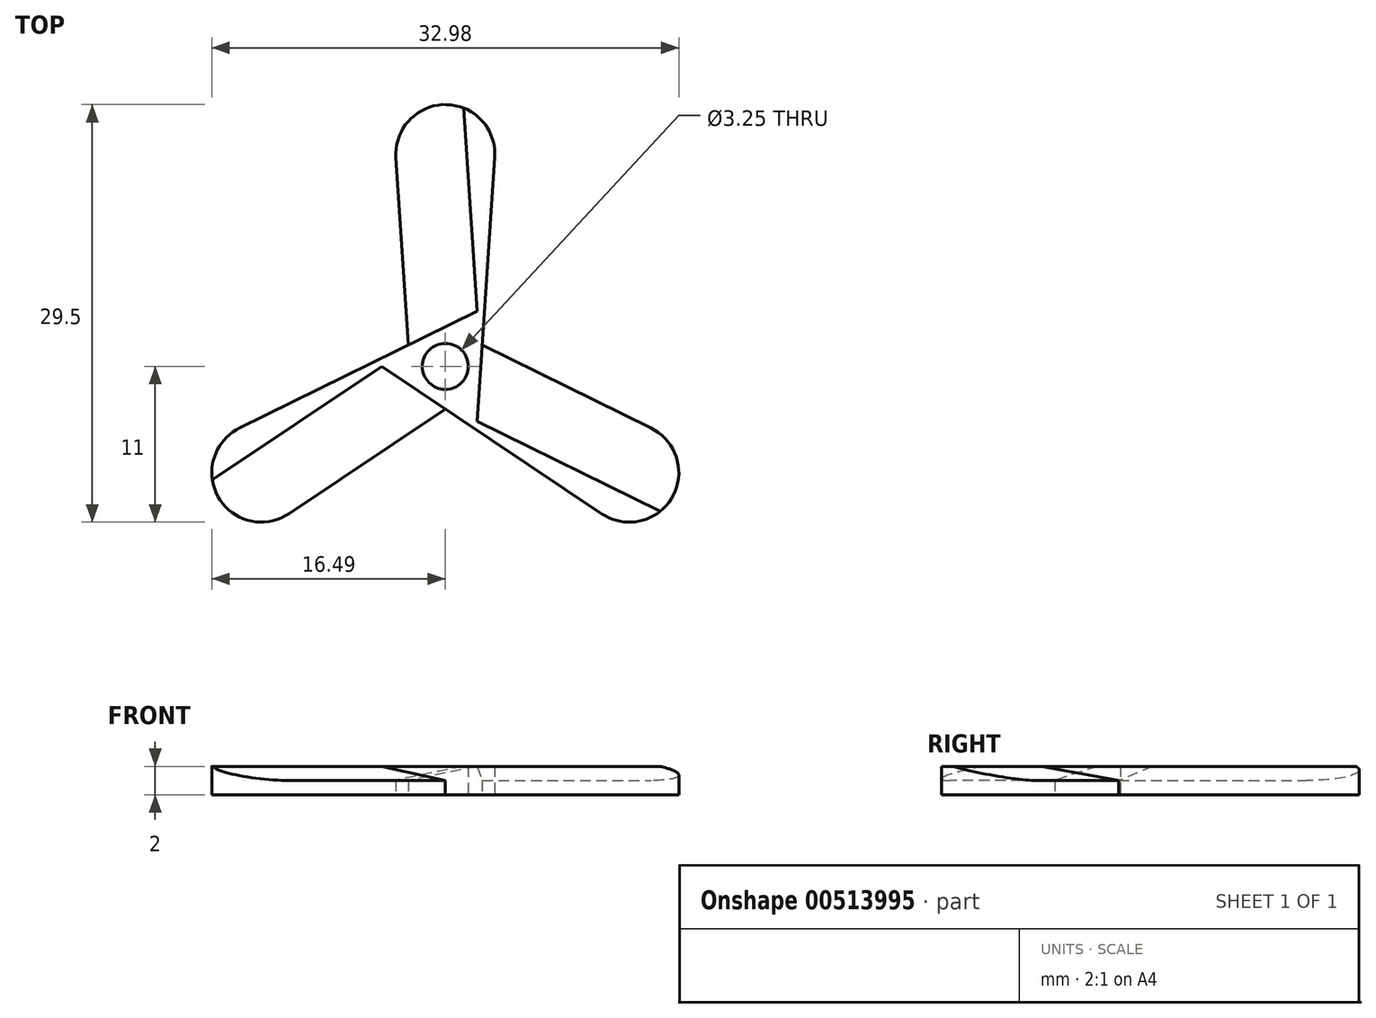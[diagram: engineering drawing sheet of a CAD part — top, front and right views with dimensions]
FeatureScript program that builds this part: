
annotation { "Feature Type Name" : "Feature", "Feature Type Description" : "" }
export const myFeature = defineFeature(function(context is Context, id is Id, definition is map)
    precondition{}
    {
        {
            var Q0;
            Q0=qCreatedBy(makeId("Top.planeOp"),FACE);
            var sketch = newSketch(context, id + "F0", { "sketchPlane" : qUnion([Q0])});
            skCircle(sketch, "E0", {"center": v(0, 0) * mm, "radius": 1.63 * mm});
            skCircle(sketch, "E1", {"center": v(0, 0) * mm, "radius": 2.5 * mm});
            skLineSegment(sketch, "E2", {"start": v(0, 0) * mm, "end": v(0, 30) * mm, "construction": true});
            skLineSegment(sketch, "E3", {"start": v(0, 0) * mm, "end": v(25.98, -15) * mm, "construction": true});
            skLineSegment(sketch, "E4", {"start": v(0, 0) * mm, "end": v(-25.98, -15) * mm, "construction": true});
            skCircle(sketch, "E5", {"center": v(0, 15) * mm, "radius": 3.5 * mm});
            skLineSegment(sketch, "E6", {"start": v(3.5, 14.77) * mm, "end": v(2.5, -0.17) * mm});
            skLineSegment(sketch, "E7", {"start": v(-3.5, 14.77) * mm, "end": v(-2.5, -0.17) * mm});
            skCircle(sketch, "E8.1.0", {"center": v(-13, -7.5) * mm, "radius": 3.5 * mm});
            skLineSegment(sketch, "E8.1.1", {"start": v(-14.53, -4.36) * mm, "end": v(-1.1, 2.24) * mm});
            skLineSegment(sketch, "E8.1.2", {"start": v(-11.04, -10.4) * mm, "end": v(1.4, -2.08) * mm});
            skCircle(sketch, "E8.2.0", {"center": v(13, -7.5) * mm, "radius": 3.5 * mm});
            skLineSegment(sketch, "E8.2.1", {"start": v(11.04, -10.4) * mm, "end": v(-1.4, -2.08) * mm});
            skLineSegment(sketch, "E8.2.2", {"start": v(14.53, -4.36) * mm, "end": v(1.1, 2.24) * mm});
            skSolve(sketch);
        }
        {
            var Q0;
            {var subQ0=sQuery(id+"F0.wireOp",EDGE,"E5");var subQ1=makeQuery(id+"F0.imprint","INTERSECT",VERTEX,{"derivedFrom":[subQ0,sQuery(id+"F0.wireOp",EDGE,"E6")]});Q0=makeQuery(id+"F0.imprint","IMPRINT",FACE,{"disambiguationData":[TD([[makeQuery(id+"F0.imprint","IMPRINT",EDGE,{"disambiguationData":[TD([[subQ1,1.0]])],"derivedFrom":subQ0}),1.0]])]});}
            var Q1;
            {var subQ7=sQuery(id+"F0.wireOp",EDGE,"E8.1.1");var subQ9=sQuery(id+"F0.wireOp",EDGE,"E1");var subQ10=makeQuery(id+"F0.imprint","INTERSECT",VERTEX,{"derivedFrom":[subQ9,subQ7]});Q1=makeQuery(id+"F0.imprint","IMPRINT",FACE,{"disambiguationData":[TD([[makeQuery(id+"F0.imprint","IMPRINT",EDGE,{"disambiguationData":[TD([[subQ10,1.0]])],"derivedFrom":subQ9}),-1.0]])]});}
            var Q2;
            {var subQ6=sQuery(id+"F0.wireOp",EDGE,"E1");var subQ9=sQuery(id+"F0.wireOp",EDGE,"E6");var subQ10=makeQuery(id+"F0.imprint","INTERSECT",VERTEX,{"derivedFrom":[subQ6,subQ9]});Q2=makeQuery(id+"F0.imprint","IMPRINT",FACE,{"disambiguationData":[TD([[makeQuery(id+"F0.imprint","IMPRINT",EDGE,{"disambiguationData":[TD([[subQ10,1.0]])],"derivedFrom":subQ6}),-1.0]])]});}
            var Q3;
            {var subQ0=sQuery(id+"F0.wireOp",EDGE,"E8.2.0");var subQ1=makeQuery(id+"F0.imprint","INTERSECT",VERTEX,{"derivedFrom":[subQ0,sQuery(id+"F0.wireOp",EDGE,"E8.2.1")]});Q3=makeQuery(id+"F0.imprint","IMPRINT",FACE,{"disambiguationData":[TD([[makeQuery(id+"F0.imprint","IMPRINT",EDGE,{"disambiguationData":[TD([[subQ1,1.0]])],"derivedFrom":subQ0}),1.0]])]});}
            var Q4;
            {var subQ3=sQuery(id+"F0.wireOp",EDGE,"E7");var subQ5=sQuery(id+"F0.wireOp",EDGE,"E1");var subQ6=makeQuery(id+"F0.imprint","INTERSECT",VERTEX,{"derivedFrom":[subQ5,subQ3]});Q4=makeQuery(id+"F0.imprint","IMPRINT",FACE,{"disambiguationData":[TD([[makeQuery(id+"F0.imprint","IMPRINT",EDGE,{"disambiguationData":[TD([[subQ6,-1.0]])],"derivedFrom":subQ5}),-1.0]])]});}
            var Q5;
            {var subQ0=sQuery(id+"F0.wireOp",EDGE,"E8.1.0");var subQ1=makeQuery(id+"F0.imprint","INTERSECT",VERTEX,{"derivedFrom":[subQ0,sQuery(id+"F0.wireOp",EDGE,"E8.1.1")]});Q5=makeQuery(id+"F0.imprint","IMPRINT",FACE,{"disambiguationData":[TD([[makeQuery(id+"F0.imprint","IMPRINT",EDGE,{"disambiguationData":[TD([[subQ1,1.0]])],"derivedFrom":subQ0}),1.0]])]});}
            var Q6;
            {var subQ0=sQuery(id+"F0.wireOp",EDGE,"E6");var subQ1=sQuery(id+"F0.wireOp",EDGE,"E1");var subQ2=makeQuery(id+"F0.imprint","INTERSECT",VERTEX,{"derivedFrom":[subQ1,subQ0]});Q6=makeQuery(id+"F0.imprint","IMPRINT",FACE,{"disambiguationData":[TD([[makeQuery(id+"F0.imprint","IMPRINT",EDGE,{"disambiguationData":[TD([[subQ2,-1.0]])],"derivedFrom":subQ1}),-1.0]])]});}
            var Q7;
            {var subQ0=sQuery(id+"F0.wireOp",EDGE,"E7");var subQ1=sQuery(id+"F0.wireOp",EDGE,"E1");var subQ2=makeQuery(id+"F0.imprint","INTERSECT",VERTEX,{"derivedFrom":[subQ1,subQ0]});Q7=makeQuery(id+"F0.imprint","IMPRINT",FACE,{"disambiguationData":[TD([[makeQuery(id+"F0.imprint","IMPRINT",EDGE,{"disambiguationData":[TD([[subQ2,1.0]])],"derivedFrom":subQ1}),-1.0]])]});}
            var Q8;
            {var subQ0=sQuery(id+"F0.wireOp",EDGE,"E8.1.2");var subQ1=sQuery(id+"F0.wireOp",EDGE,"E1");var subQ2=makeQuery(id+"F0.imprint","INTERSECT",VERTEX,{"derivedFrom":[subQ1,subQ0]});Q8=makeQuery(id+"F0.imprint","IMPRINT",FACE,{"disambiguationData":[TD([[makeQuery(id+"F0.imprint","IMPRINT",EDGE,{"disambiguationData":[TD([[subQ2,1.0]])],"derivedFrom":subQ1}),-1.0]])]});}
            var Q9;
            Q9=makeQuery(id+"F0.imprint","IMPRINT",FACE,{"disambiguationData":[TD([[makeQuery(id+"F0.imprint","IMPRINT",EDGE,{"derivedFrom":sQuery(id+"F0.wireOp",EDGE,"E0")}),-1.0]])]});
            extrude(context, id + "F1", {"entities" : qUnion([Q0, Q1, Q2, Q3, Q4, Q5, Q6, Q7, Q8, Q9]), "depth" : 2 * mm});
        }
        {
            var Q0;
            Q0=makeQuery(id+"F1.opExtrude","CAP_EDGE",EDGE,{"disambiguationData":[OSD([sQuery(id+"F0.wireOp",EDGE,"E7")])],"isStart":false});
            var Q1;
            Q1=makeQuery(id+"F1.opExtrude","CAP_EDGE",EDGE,{"disambiguationData":[OSD([sQuery(id+"F0.wireOp",EDGE,"E8.1.2")])],"isStart":false});
            var Q2;
            Q2=makeQuery(id+"F1.opExtrude","CAP_EDGE",EDGE,{"disambiguationData":[OSD([sQuery(id+"F0.wireOp",EDGE,"E8.2.2")])],"isStart":false});
            chamfer(context, id + "F2", {"entities" : qUnion([Q0, Q1, Q2]), "chamferType" : ChamferType.TWO_OFFSETS, "width1" : 5 * mm, "oppositeDirection" : false, "width2" : 1 * mm});
        }
    });
